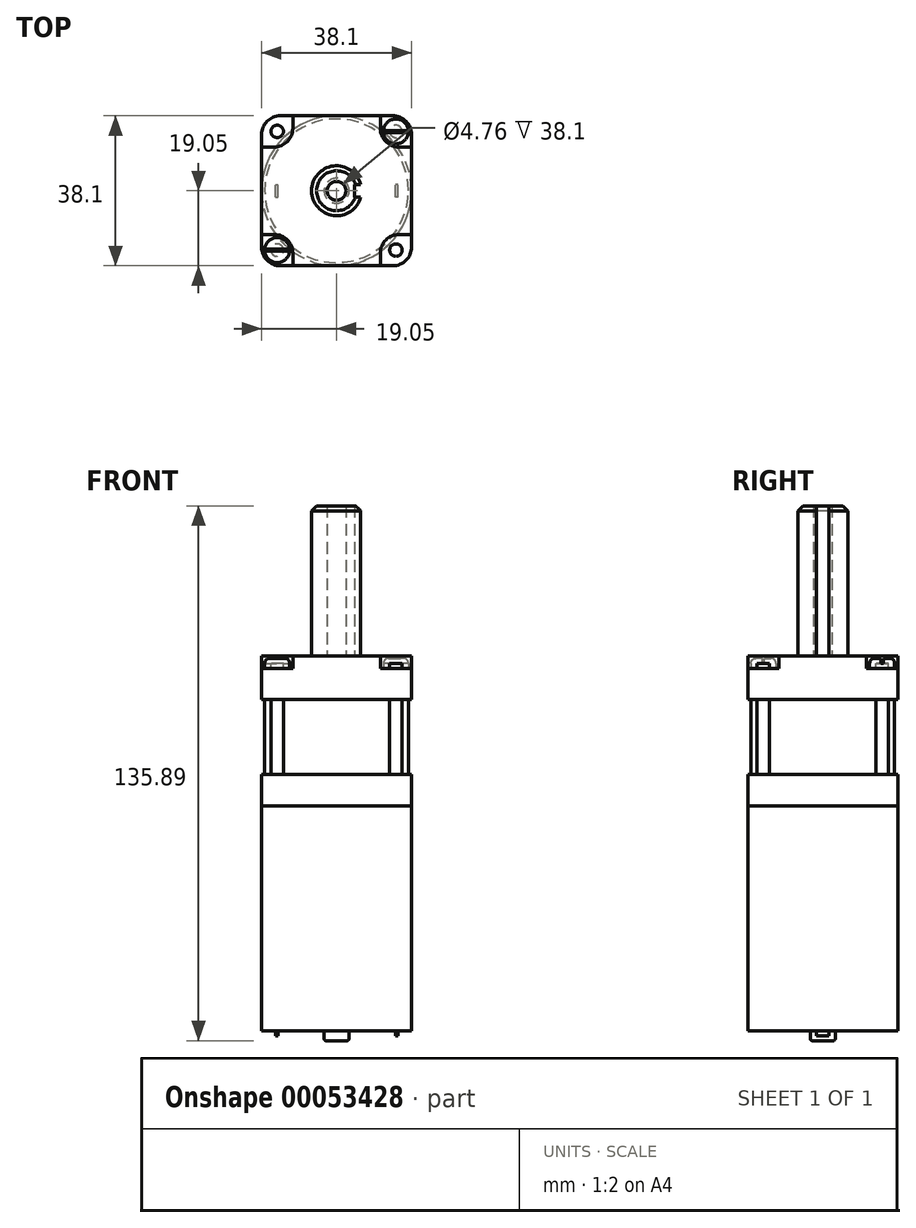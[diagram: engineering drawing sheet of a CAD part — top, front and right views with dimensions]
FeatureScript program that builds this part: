
annotation { "Feature Type Name" : "Feature", "Feature Type Description" : "" }
export const myFeature = defineFeature(function(context is Context, id is Id, definition is map)
    precondition{}
    {
        {
            var Q0;
            Q0=qCreatedBy(makeId("Top.planeOp"),FACE);
            var sketch = newSketch(context, id + "F0", { "sketchPlane" : qUnion([Q0])});
            skLineSegment(sketch, "E0.rect.bottom", {"start": v(-19.05, 19.05) * mm, "end": v(19.05, 19.05) * mm});
            skLineSegment(sketch, "E0.rect.top", {"start": v(-19.05, -19.05) * mm, "end": v(19.05, -19.05) * mm});
            skLineSegment(sketch, "E0.rect.left", {"start": v(-19.05, 19.05) * mm, "end": v(-19.05, -19.05) * mm});
            skLineSegment(sketch, "E0.rect.right", {"start": v(19.05, 19.05) * mm, "end": v(19.05, -19.05) * mm});
            skPoint(sketch, "E0.rect.middle", {"position": v(0, 0) * mm});
            skSolve(sketch);
        }
        {
            var Q0;
            Q0=qSketchRegion(id+"F0",true);
            extrude(context, id + "F1", {"entities" : qUnion([Q0]), "depth" : 7.94 * mm});
        }
        {
            var Q0;
            Q0=makeQuery(id+"F1.opExtrude","CAP_FACE",FACE,{"disambiguationData":[OSD([sQuery(id+"F0.wireOp",EDGE,"E0.rect.bottom"),sQuery(id+"F0.wireOp",EDGE,"E0.rect.top"),sQuery(id+"F0.wireOp",EDGE,"E0.rect.left"),sQuery(id+"F0.wireOp",EDGE,"E0.rect.right")])],"isStart":false});
            var sketch = newSketch(context, id + "F2", { "sketchPlane" : qUnion([Q0])});
            skCircle(sketch, "E1", {"center": v(0, 0) * mm, "radius": 18.26 * mm});
            skSolve(sketch);
        }
        {
            var Q0;
            Q0=makeQuery(id+"F2.imprint","IMPRINT",FACE,{"disambiguationData":[TD([[makeQuery(id+"F2.imprint","IMPRINT",EDGE,{"derivedFrom":sQuery(id+"F2.wireOp",EDGE,"E1")}),1.0]])]});
            extrude(context, id + "F3", {"entities" : qUnion([Q0]), "operationType" : NewBodyOperationType.ADD, "depth" : 19.05 * mm});
        }
        {
            var Q0;
            Q0=makeQuery(id+"F1.opExtrude","CAP_FACE",FACE,{"disambiguationData":[OSD([sQuery(id+"F0.wireOp",EDGE,"E0.rect.bottom"),sQuery(id+"F0.wireOp",EDGE,"E0.rect.top"),sQuery(id+"F0.wireOp",EDGE,"E0.rect.left"),sQuery(id+"F0.wireOp",EDGE,"E0.rect.right")])],"isStart":true});
            var sketch = newSketch(context, id + "F4", { "sketchPlane" : qUnion([Q0])});
            skCircle(sketch, "E2", {"center": v(0, 0) * mm, "radius": 19.05 * mm});
            skSolve(sketch);
        }
        {
            var Q0;
            {var subQ0=sQuery(id+"F4.wireOp",EDGE,"E2");var subQ1=makeQuery(id+"F4.imprint","INTERSECT",VERTEX,{"derivedFrom":[makeQuery(id+"F1.opExtrude","CAP_EDGE",EDGE,{"disambiguationData":[OSD([sQuery(id+"F0.wireOp",EDGE,"E0.rect.top")])],"isStart":true}),subQ0]});Q0=makeQuery(id+"F4.imprint","IMPRINT",FACE,{"disambiguationData":[TD([[makeQuery(id+"F4.imprint","IMPRINT",EDGE,{"disambiguationData":[TD([[subQ1,1.0]])],"derivedFrom":subQ0}),1.0]])]});}
            extrude(context, id + "F5", {"entities" : qUnion([Q0]), "operationType" : NewBodyOperationType.ADD, "depth" : 57.15 * mm});
        }
        {
            var Q0;
            Q0=makeQuery(id+"F3.opExtrude","CAP_FACE",FACE,{"disambiguationData":[OSD([sQuery(id+"F2.wireOp",EDGE,"E1")])],"isStart":false});
            var sketch = newSketch(context, id + "F6", { "sketchPlane" : qUnion([Q0])});
            skLineSegment(sketch, "E3.rect.bottom", {"start": v(19.05, -19.05) * mm, "end": v(-19.05, -19.05) * mm});
            skLineSegment(sketch, "E3.rect.top", {"start": v(19.05, 19.05) * mm, "end": v(-19.05, 19.05) * mm});
            skLineSegment(sketch, "E3.rect.left", {"start": v(19.05, -19.05) * mm, "end": v(19.05, 19.05) * mm});
            skLineSegment(sketch, "E3.rect.right", {"start": v(-19.05, -19.05) * mm, "end": v(-19.05, 19.05) * mm});
            skPoint(sketch, "E3.rect.middle", {"position": v(0, 0) * mm});
            skSolve(sketch);
        }
        {
            var Q0;
            Q0=qSketchRegion(id+"F6",true);
            extrude(context, id + "F7", {"entities" : qUnion([Q0]), "operationType" : NewBodyOperationType.ADD, "depth" : 11.1 * mm});
        }
        {
            var Q0;
            Q0=makeQuery(id+"F7.opExtrude","CAP_FACE",FACE,{"disambiguationData":[OSD([sQuery(id+"F6.wireOp",EDGE,"E3.rect.bottom"),sQuery(id+"F6.wireOp",EDGE,"E3.rect.top"),sQuery(id+"F6.wireOp",EDGE,"E3.rect.left"),sQuery(id+"F6.wireOp",EDGE,"E3.rect.right")])],"isStart":false});
            var sketch = newSketch(context, id + "F8", { "sketchPlane" : qUnion([Q0])});
            skLineSegment(sketch, "E4", {"start": v(-19.05, -11.11) * mm, "end": v(-11.11, -11.11) * mm});
            skLineSegment(sketch, "E5", {"start": v(-11.11, -11.11) * mm, "end": v(-11.11, -19.05) * mm});
            skLineSegment(sketch, "E6", {"start": v(-11.11, -19.05) * mm, "end": v(-19.05, -19.05) * mm});
            skLineSegment(sketch, "E7", {"start": v(-19.05, -19.05) * mm, "end": v(-19.05, -11.11) * mm});
            skLineSegment(sketch, "E8.MirrorCS", {"start": v(11.11, -11.11) * mm, "end": v(11.11, -19.05) * mm});
            skLineSegment(sketch, "E9.MirrorCS", {"start": v(19.05, -11.11) * mm, "end": v(11.11, -11.11) * mm});
            skLineSegment(sketch, "E10.MirrorCS", {"start": v(19.05, -19.05) * mm, "end": v(19.05, -11.11) * mm});
            skLineSegment(sketch, "E11.MirrorCS", {"start": v(11.11, -19.05) * mm, "end": v(19.05, -19.05) * mm});
            skLineSegment(sketch, "E12.MirrorCS", {"start": v(19.05, 11.11) * mm, "end": v(11.11, 11.11) * mm});
            skLineSegment(sketch, "E13.MirrorCS", {"start": v(11.11, 11.11) * mm, "end": v(11.11, 19.05) * mm});
            skLineSegment(sketch, "E14.MirrorCS", {"start": v(11.11, 19.05) * mm, "end": v(19.05, 19.05) * mm});
            skLineSegment(sketch, "E15.MirrorCS", {"start": v(19.05, 19.05) * mm, "end": v(19.05, 11.11) * mm});
            skLineSegment(sketch, "E16.MirrorCS", {"start": v(-19.05, 11.11) * mm, "end": v(-11.11, 11.11) * mm});
            skLineSegment(sketch, "E17.MirrorCS", {"start": v(-11.11, 11.11) * mm, "end": v(-11.11, 19.05) * mm});
            skLineSegment(sketch, "E18.MirrorCS", {"start": v(-11.11, 19.05) * mm, "end": v(-19.05, 19.05) * mm});
            skLineSegment(sketch, "E19.MirrorCS", {"start": v(-19.05, 19.05) * mm, "end": v(-19.05, 11.11) * mm});
            skSolve(sketch);
        }
        {
            var Q0;
            Q0=makeQuery(id+"F8.imprint","IMPRINT",FACE,{"disambiguationData":[TD([[makeQuery(id+"F8.imprint","IMPRINT",EDGE,{"derivedFrom":sQuery(id+"F8.wireOp",EDGE,"E16.MirrorCS")}),1.0]])]});
            var Q1;
            Q1=makeQuery(id+"F8.imprint","IMPRINT",FACE,{"disambiguationData":[TD([[makeQuery(id+"F8.imprint","IMPRINT",EDGE,{"derivedFrom":sQuery(id+"F8.wireOp",EDGE,"E12.MirrorCS")}),-1.0]])]});
            var Q2;
            Q2=makeQuery(id+"F8.imprint","IMPRINT",FACE,{"disambiguationData":[TD([[makeQuery(id+"F8.imprint","IMPRINT",EDGE,{"derivedFrom":sQuery(id+"F8.wireOp",EDGE,"E8.MirrorCS")}),1.0]])]});
            var Q3;
            Q3=makeQuery(id+"F8.imprint","IMPRINT",FACE,{"disambiguationData":[TD([[makeQuery(id+"F8.imprint","IMPRINT",EDGE,{"derivedFrom":sQuery(id+"F8.wireOp",EDGE,"E4")}),-1.0]])]});
            extrude(context, id + "F9", {"entities" : qUnion([Q0, Q1, Q2, Q3]), "operationType" : NewBodyOperationType.REMOVE, "oppositeDirection" : true, "depth" : 3.17 * mm});
        }
        {
            var Q0;
            Q0=makeQuery(id+"F7.opExtrude","SWEPT_EDGE",EDGE,{"disambiguationData":[OSD([sQuery(id+"F6.wireOp",EDGE,"E3.rect.bottom"),sQuery(id+"F6.wireOp",EDGE,"E3.rect.right")])]});
            var Q1;
            Q1=makeQuery(id+"F7.opExtrude","SWEPT_EDGE",EDGE,{"disambiguationData":[OSD([sQuery(id+"F6.wireOp",EDGE,"E3.rect.bottom"),sQuery(id+"F6.wireOp",EDGE,"E3.rect.left")])]});
            var Q2;
            Q2=makeQuery(id+"F1.opExtrude","SWEPT_EDGE",EDGE,{"disambiguationData":[OSD([sQuery(id+"F0.wireOp",EDGE,"E0.rect.top"),sQuery(id+"F0.wireOp",EDGE,"E0.rect.right")])]});
            var Q3;
            Q3=makeQuery(id+"F1.opExtrude","SWEPT_EDGE",EDGE,{"disambiguationData":[OSD([sQuery(id+"F0.wireOp",EDGE,"E0.rect.top"),sQuery(id+"F0.wireOp",EDGE,"E0.rect.left")])]});
            var Q4;
            Q4=makeQuery(id+"F1.opExtrude","SWEPT_EDGE",EDGE,{"disambiguationData":[OSD([sQuery(id+"F0.wireOp",EDGE,"E0.rect.bottom"),sQuery(id+"F0.wireOp",EDGE,"E0.rect.right")])]});
            var Q5;
            Q5=makeQuery(id+"F7.opExtrude","SWEPT_EDGE",EDGE,{"disambiguationData":[OSD([sQuery(id+"F6.wireOp",EDGE,"E3.rect.top"),sQuery(id+"F6.wireOp",EDGE,"E3.rect.left")])]});
            var Q6;
            Q6=makeQuery(id+"F1.opExtrude","SWEPT_EDGE",EDGE,{"disambiguationData":[OSD([sQuery(id+"F0.wireOp",EDGE,"E0.rect.bottom"),sQuery(id+"F0.wireOp",EDGE,"E0.rect.left")])]});
            var Q7;
            Q7=makeQuery(id+"F7.opExtrude","SWEPT_EDGE",EDGE,{"disambiguationData":[OSD([sQuery(id+"F6.wireOp",EDGE,"E3.rect.top"),sQuery(id+"F6.wireOp",EDGE,"E3.rect.right")])]});
            fillet(context, id + "F10", {"entities" : qUnion([Q0, Q1, Q2, Q3, Q4, Q5, Q6, Q7]), "radius" : 4.76 * mm, "tangentPropagation" : true, "allowEdgeOverflow" : false});
        }
        {
            var Q0;
            Q0=makeQuery(id+"F9.boolean.opBoolean","COPY",EDGE,{"derivedFrom":makeQuery(id+"F9.opExtrude","SWEPT_EDGE",EDGE,{"disambiguationData":[OSD([sQuery(id+"F8.wireOp",EDGE,"E8.MirrorCS"),sQuery(id+"F8.wireOp",EDGE,"E9.MirrorCS")])]})});
            var Q1;
            Q1=makeQuery(id+"F9.boolean.opBoolean","COPY",EDGE,{"derivedFrom":makeQuery(id+"F9.opExtrude","SWEPT_EDGE",EDGE,{"disambiguationData":[OSD([sQuery(id+"F8.wireOp",EDGE,"E4"),sQuery(id+"F8.wireOp",EDGE,"E5")])]})});
            var Q2;
            Q2=makeQuery(id+"F9.boolean.opBoolean","COPY",EDGE,{"derivedFrom":makeQuery(id+"F9.opExtrude","SWEPT_EDGE",EDGE,{"disambiguationData":[OSD([sQuery(id+"F8.wireOp",EDGE,"E12.MirrorCS"),sQuery(id+"F8.wireOp",EDGE,"E13.MirrorCS")])]})});
            var Q3;
            Q3=makeQuery(id+"F9.boolean.opBoolean","COPY",EDGE,{"derivedFrom":makeQuery(id+"F9.opExtrude","SWEPT_EDGE",EDGE,{"disambiguationData":[OSD([sQuery(id+"F8.wireOp",EDGE,"E16.MirrorCS"),sQuery(id+"F8.wireOp",EDGE,"E17.MirrorCS")])]})});
            fillet(context, id + "F11", {"entities" : qUnion([Q0, Q1, Q2, Q3]), "radius" : 4.76 * mm, "tangentPropagation" : true, "allowEdgeOverflow" : false});
        }
        {
            var Q0;
            Q0=makeQuery(id+"F9.boolean.opBoolean","COPY",FACE,{"derivedFrom":makeQuery(id+"F9.opExtrude","CAP_FACE",FACE,{"disambiguationData":[OSD([sQuery(id+"F8.wireOp",EDGE,"E12.MirrorCS"),sQuery(id+"F8.wireOp",EDGE,"E13.MirrorCS"),sQuery(id+"F8.wireOp",EDGE,"E14.MirrorCS"),sQuery(id+"F8.wireOp",EDGE,"E15.MirrorCS")])],"isStart":false})});
            var sketch = newSketch(context, id + "F12", { "sketchPlane" : qUnion([Q0])});
            skCircle(sketch, "E20", {"center": v(15.08, 15.08) * mm, "radius": 3.18 * mm});
            skCircle(sketch, "E21.MirrorC", {"center": v(-15.08, 15.08) * mm, "radius": 3.18 * mm});
            skCircle(sketch, "E22.MirrorC", {"center": v(-15.08, -15.08) * mm, "radius": 3.18 * mm});
            skCircle(sketch, "E23.MirrorC", {"center": v(15.08, -15.08) * mm, "radius": 3.18 * mm});
            skSolve(sketch);
        }
        {
            var Q0;
            Q0=makeQuery(id+"F12.imprint","IMPRINT",FACE,{"disambiguationData":[TD([[makeQuery(id+"F12.imprint","IMPRINT",EDGE,{"derivedFrom":sQuery(id+"F12.wireOp",EDGE,"E20")}),1.0]])]});
            var Q1;
            Q1=makeQuery(id+"F12.imprint","IMPRINT",FACE,{"disambiguationData":[TD([[makeQuery(id+"F12.imprint","IMPRINT",EDGE,{"derivedFrom":sQuery(id+"F12.wireOp",EDGE,"E21.MirrorC")}),-1.0]])]});
            var Q2;
            Q2=makeQuery(id+"F12.imprint","IMPRINT",FACE,{"disambiguationData":[TD([[makeQuery(id+"F12.imprint","IMPRINT",EDGE,{"derivedFrom":sQuery(id+"F12.wireOp",EDGE,"E22.MirrorC")}),1.0]])]});
            var Q3;
            Q3=makeQuery(id+"F12.imprint","IMPRINT",FACE,{"disambiguationData":[TD([[makeQuery(id+"F12.imprint","IMPRINT",EDGE,{"derivedFrom":sQuery(id+"F12.wireOp",EDGE,"E23.MirrorC")}),-1.0]])]});
            extrude(context, id + "F13", {"entities" : qUnion([Q0, Q1, Q2, Q3]), "operationType" : NewBodyOperationType.ADD, "depth" : 2.54 * mm});
        }
        {
            var Q0;
            Q0=makeQuery(id+"F13.opExtrude","CAP_EDGE",EDGE,{"disambiguationData":[OSD([sQuery(id+"F12.wireOp",EDGE,"E21.MirrorC")])],"isStart":false});
            var Q1;
            Q1=makeQuery(id+"F13.opExtrude","CAP_EDGE",EDGE,{"disambiguationData":[OSD([sQuery(id+"F12.wireOp",EDGE,"E20")])],"isStart":false});
            var Q2;
            Q2=makeQuery(id+"F13.opExtrude","CAP_EDGE",EDGE,{"disambiguationData":[OSD([sQuery(id+"F12.wireOp",EDGE,"E23.MirrorC")])],"isStart":false});
            var Q3;
            Q3=makeQuery(id+"F13.opExtrude","CAP_EDGE",EDGE,{"disambiguationData":[OSD([sQuery(id+"F12.wireOp",EDGE,"E22.MirrorC")])],"isStart":false});
            fillet(context, id + "F14", {"entities" : qUnion([Q0, Q1, Q2, Q3]), "radius" : 1.27 * mm, "tangentPropagation" : true, "allowEdgeOverflow" : false});
        }
        {
            var Q0;
            Q0=makeQuery(id+"F13.opExtrude","CAP_FACE",FACE,{"disambiguationData":[OSD([sQuery(id+"F12.wireOp",EDGE,"E20")])],"isStart":false});
            var sketch = newSketch(context, id + "F15", { "sketchPlane" : qUnion([Q0])});
            skLineSegment(sketch, "E24.rect.bottom", {"start": v(18.39, 15.34) * mm, "end": v(11.78, 15.34) * mm});
            skLineSegment(sketch, "E24.rect.top", {"start": v(18.39, 14.82) * mm, "end": v(11.78, 14.82) * mm});
            skLineSegment(sketch, "E24.rect.left", {"start": v(18.39, 15.34) * mm, "end": v(18.39, 14.82) * mm});
            skLineSegment(sketch, "E24.rect.right", {"start": v(11.78, 15.34) * mm, "end": v(11.78, 14.82) * mm});
            skPoint(sketch, "E24.rect.middle", {"position": v(15.08, 15.08) * mm});
            skLineSegment(sketch, "E25.MirrorCS", {"start": v(-18.39, 15.34) * mm, "end": v(-11.78, 15.34) * mm});
            skLineSegment(sketch, "E26.MirrorCS", {"start": v(-18.39, 14.82) * mm, "end": v(-11.78, 14.82) * mm});
            skLineSegment(sketch, "E27.MirrorCS", {"start": v(-11.78, 15.34) * mm, "end": v(-11.78, 14.82) * mm});
            skLineSegment(sketch, "E28.MirrorCS", {"start": v(-18.39, 15.34) * mm, "end": v(-18.39, 14.82) * mm});
            skLineSegment(sketch, "E29.MirrorCS", {"start": v(18.39, -15.34) * mm, "end": v(11.78, -15.34) * mm});
            skLineSegment(sketch, "E30.MirrorCS", {"start": v(18.39, -14.82) * mm, "end": v(11.78, -14.82) * mm});
            skLineSegment(sketch, "E31.MirrorCS", {"start": v(11.78, -15.34) * mm, "end": v(11.78, -14.82) * mm});
            skLineSegment(sketch, "E32.MirrorCS", {"start": v(18.39, -15.34) * mm, "end": v(18.39, -14.82) * mm});
            skLineSegment(sketch, "E33.MirrorCS", {"start": v(-18.39, -14.82) * mm, "end": v(-11.78, -14.82) * mm});
            skLineSegment(sketch, "E34.MirrorCS", {"start": v(-18.39, -15.34) * mm, "end": v(-11.78, -15.34) * mm});
            skLineSegment(sketch, "E35.MirrorCS", {"start": v(-11.78, -15.34) * mm, "end": v(-11.78, -14.82) * mm});
            skLineSegment(sketch, "E36.MirrorCS", {"start": v(-18.39, -15.34) * mm, "end": v(-18.39, -14.82) * mm});
            skSolve(sketch);
        }
        {
            var Q0;
            Q0=qSketchRegion(id+"F15",true);
            extrude(context, id + "F16", {"entities" : qUnion([Q0]), "operationType" : NewBodyOperationType.REMOVE, "oppositeDirection" : true, "depth" : 1.27 * mm});
        }
        {
            var Q0;
            Q0=makeQuery(id+"F16.boolean.opBoolean","COPY",FACE,{"derivedFrom":makeQuery(id+"F16.opExtrude","CAP_FACE",FACE,{"disambiguationData":[OSD([sQuery(id+"F15.wireOp",EDGE,"E24.rect.bottom"),sQuery(id+"F15.wireOp",EDGE,"E24.rect.top"),sQuery(id+"F15.wireOp",EDGE,"E24.rect.left"),sQuery(id+"F15.wireOp",EDGE,"E24.rect.right")])],"isStart":false})});
            var sketch = newSketch(context, id + "F17", { "sketchPlane" : qUnion([Q0])});
            skCircle(sketch, "E37", {"center": v(15.08, 15.08) * mm, "radius": 1.59 * mm});
            skCircle(sketch, "E38.MirrorC", {"center": v(-15.08, 15.08) * mm, "radius": 1.59 * mm});
            skCircle(sketch, "E39.MirrorC", {"center": v(-15.08, -15.08) * mm, "radius": 1.59 * mm});
            skCircle(sketch, "E40.MirrorC", {"center": v(15.08, -15.08) * mm, "radius": 1.59 * mm});
            skSolve(sketch);
        }
        {
            var Q0;
            Q0=qSketchRegion(id+"F17",true);
            var Q1;
            Q1=makeQuery(id+"F1.opExtrude","CAP_FACE",FACE,{"disambiguationData":[OSD([sQuery(id+"F0.wireOp",EDGE,"E0.rect.bottom"),sQuery(id+"F0.wireOp",EDGE,"E0.rect.top"),sQuery(id+"F0.wireOp",EDGE,"E0.rect.left"),sQuery(id+"F0.wireOp",EDGE,"E0.rect.right")])],"isStart":false});
            extrude(context, id + "F18", {"entities" : qUnion([Q0]), "operationType" : NewBodyOperationType.ADD, "endBound" : BoundingType.UP_TO_SURFACE, "oppositeDirection" : true, "endBoundEntityFace" : qUnion([Q1]), "depth" : 25.4 * mm});
        }
        {
            var Q0;
            Q0=makeQuery(id+"F5.opExtrude","CAP_FACE",FACE,{"disambiguationData":[OSD([sQuery(id+"F4.wireOp",EDGE,"E2")])],"isStart":false});
            var sketch = newSketch(context, id + "F19", { "sketchPlane" : qUnion([Q0])});
            skCircle(sketch, "E41", {"center": v(0, 0) * mm, "radius": 3.18 * mm});
            skLineSegment(sketch, "E42.rect.bottom", {"start": v(15.56, 1.59) * mm, "end": v(14.92, 1.59) * mm});
            skLineSegment(sketch, "E42.rect.top", {"start": v(15.56, -1.59) * mm, "end": v(14.92, -1.59) * mm});
            skLineSegment(sketch, "E42.rect.left", {"start": v(15.56, 1.59) * mm, "end": v(15.56, -1.59) * mm});
            skLineSegment(sketch, "E42.rect.right", {"start": v(14.92, 1.59) * mm, "end": v(14.92, -1.59) * mm});
            skPoint(sketch, "E42.rect.middle", {"position": v(15.24, 0) * mm});
            skLineSegment(sketch, "E43.MirrorCS", {"start": v(-15.56, -1.59) * mm, "end": v(-14.92, -1.59) * mm});
            skLineSegment(sketch, "E44.MirrorCS", {"start": v(-15.56, 1.59) * mm, "end": v(-14.92, 1.59) * mm});
            skPoint(sketch, "E45.MirrorP", {"position": v(-15.24, 0) * mm});
            skLineSegment(sketch, "E46.MirrorCS", {"start": v(-14.92, 1.59) * mm, "end": v(-14.92, -1.59) * mm});
            skLineSegment(sketch, "E47.MirrorCS", {"start": v(-15.56, 1.59) * mm, "end": v(-15.56, -1.59) * mm});
            skSolve(sketch);
        }
        {
            var Q0;
            Q0=makeQuery(id+"F19.imprint","IMPRINT",FACE,{"disambiguationData":[TD([[makeQuery(id+"F19.imprint","IMPRINT",EDGE,{"derivedFrom":sQuery(id+"F19.wireOp",EDGE,"E41")}),1.0]])]});
            extrude(context, id + "F20", {"entities" : qUnion([Q0]), "operationType" : NewBodyOperationType.ADD, "depth" : 2.54 * mm});
        }
        {
            var Q0;
            Q0=makeQuery(id+"F7.opExtrude","CAP_FACE",FACE,{"disambiguationData":[OSD([sQuery(id+"F6.wireOp",EDGE,"E3.rect.bottom"),sQuery(id+"F6.wireOp",EDGE,"E3.rect.top"),sQuery(id+"F6.wireOp",EDGE,"E3.rect.left"),sQuery(id+"F6.wireOp",EDGE,"E3.rect.right")])],"isStart":false});
            var sketch = newSketch(context, id + "F21", { "sketchPlane" : qUnion([Q0])});
            skCircle(sketch, "E48", {"center": v(0, 0) * mm, "radius": 2.38 * mm});
            skLineSegment(sketch, "E49", {"start": v(4.56, 0) * mm, "end": v(4.56, -1.59) * mm});
            skLineSegment(sketch, "E50", {"start": v(4.56, -1.59) * mm, "end": v(6.15, -1.59) * mm});
            skLineSegment(sketch, "E51", {"start": v(4.56, 0) * mm, "end": v(4.56, 1.59) * mm});
            skLineSegment(sketch, "E52", {"start": v(4.56, 1.59) * mm, "end": v(6.15, 1.59) * mm});
            skArc(sketch, "E53", {"start": v(6.15, 1.59) * mm, "mid": v(-6.35, 0) * mm, "end": v(6.15, -1.59) * mm});
            skSolve(sketch);
        }
        {
            var Q0;
            Q0=qSketchRegion(id+"F19",true);
            extrude(context, id + "F22", {"entities" : qUnion([Q0]), "operationType" : NewBodyOperationType.ADD, "depth" : 1.27 * mm});
        }
        {
            var Q0;
            Q0=makeQuery(id+"F20.opExtrude","SWEPT_FACE",FACE,{"disambiguationData":[OSD([sQuery(id+"F19.wireOp",EDGE,"E41")])]});
            fillet(context, id + "F23", {"entities" : qUnion([Q0]), "radius" : 0.5 * mm, "tangentPropagation" : true, "allowEdgeOverflow" : false});
        }
        {
            var Q0;
            Q0=qSketchRegion(id+"F21",true);
            extrude(context, id + "F24", {"entities" : qUnion([Q0]), "operationType" : NewBodyOperationType.ADD, "depth" : 38.1 * mm});
        }
        {
            var Q0;
            Q0=makeQuery(id+"F24.opExtrude","CAP_EDGE",EDGE,{"disambiguationData":[OSD([sQuery(id+"F21.wireOp",EDGE,"E53")])],"isStart":false});
            chamfer(context, id + "F25", {"entities" : qUnion([Q0]), "width" : 1.27 * mm, "tangentPropagation" : true});
        }
    });
